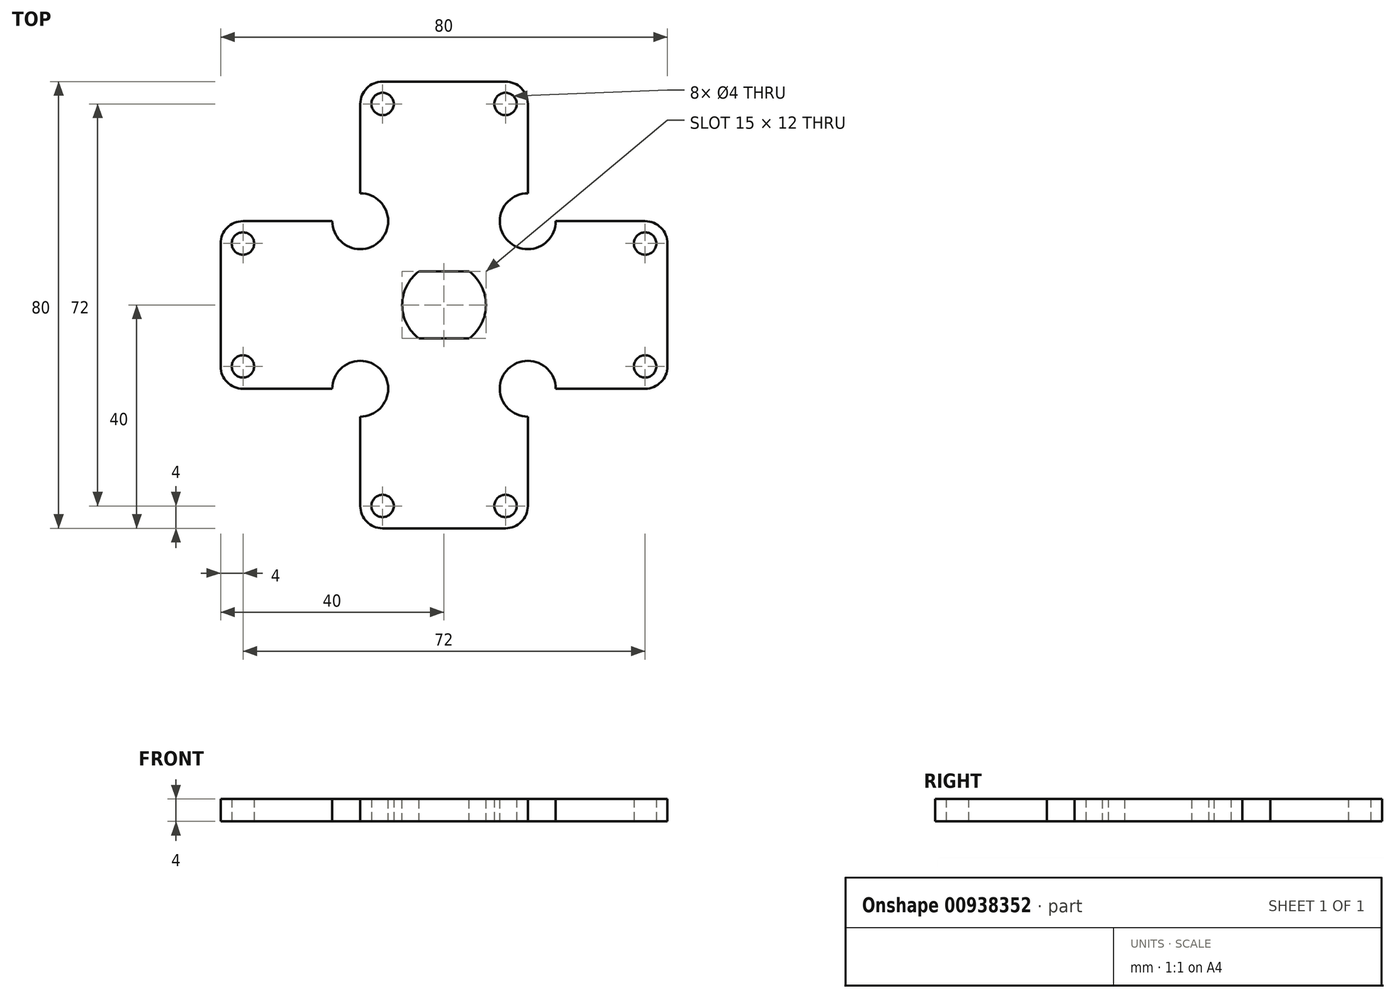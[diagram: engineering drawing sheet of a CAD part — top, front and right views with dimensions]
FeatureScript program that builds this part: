
annotation { "Feature Type Name" : "Feature", "Feature Type Description" : "" }
export const myFeature = defineFeature(function(context is Context, id is Id, definition is map)
    precondition{}
    {
        {
            var Q0;
            Q0=qCreatedBy(makeId("Top.planeOp"),FACE);
            var sketch = newSketch(context, id + "F0", { "sketchPlane" : qUnion([Q0])});
            skCircle(sketch, "E0", {"center": v(0, 0) * mm, "radius": 7.5 * mm, "construction": true});
            skLineSegment(sketch, "E1", {"start": v(-4.5, 6) * mm, "end": v(4.5, 6) * mm});
            skLineSegment(sketch, "E2", {"start": v(-4.5, -6) * mm, "end": v(4.5, -6) * mm});
            skArc(sketch, "E3", {"start": v(-4.5, 6) * mm, "mid": v(-7.5, 0) * mm, "end": v(-4.5, -6) * mm});
            skArc(sketch, "E4", {"start": v(4.5, 6) * mm, "mid": v(7.5, 0) * mm, "end": v(4.5, -6) * mm});
            skSolve(sketch);
        }
        {
            var Q0;
            Q0=qCreatedBy(makeId("Top.planeOp"),FACE);
            var sketch = newSketch(context, id + "F1", { "sketchPlane" : qUnion([Q0])});
            skLineSegment(sketch, "E5", {"start": v(0, 0) * mm, "end": v(-15, 15) * mm, "construction": true});
            skLineSegment(sketch, "E6", {"start": v(-15, 15) * mm, "end": v(-15, 36) * mm});
            skLineSegment(sketch, "E7", {"start": v(-11, 40) * mm, "end": v(0, 40) * mm});
            skArc(sketch, "E8", {"start": v(-15, 36) * mm, "mid": v(-13.83, 38.83) * mm, "end": v(-11, 40) * mm});
            skCircle(sketch, "E9", {"center": v(-11, 36) * mm, "radius": 2 * mm});
            skLineSegment(sketch, "E10.MirrorCS", {"start": v(11, 40) * mm, "end": v(0, 40) * mm});
            skArc(sketch, "E11.MirrorCS", {"start": v(15, 36) * mm, "mid": v(13.83, 38.83) * mm, "end": v(11, 40) * mm});
            skLineSegment(sketch, "E12.MirrorCS", {"start": v(15, 15) * mm, "end": v(15, 36) * mm});
            skCircle(sketch, "E13.MirrorC", {"center": v(11, 36) * mm, "radius": 2 * mm});
            skArc(sketch, "E14.1.0", {"start": v(-36, -15) * mm, "mid": v(-38.83, -13.83) * mm, "end": v(-40, -11) * mm});
            skLineSegment(sketch, "E14.1.1", {"start": v(-40, 11) * mm, "end": v(-40, 0) * mm});
            skArc(sketch, "E14.1.2", {"start": v(-36, 15) * mm, "mid": v(-38.83, 13.83) * mm, "end": v(-40, 11) * mm});
            skLineSegment(sketch, "E14.1.3", {"start": v(-15, 15) * mm, "end": v(-36, 15) * mm});
            skLineSegment(sketch, "E14.1.4", {"start": v(-40, -11) * mm, "end": v(-40, 0) * mm});
            skCircle(sketch, "E14.1.5", {"center": v(-36, -11) * mm, "radius": 2 * mm});
            skLineSegment(sketch, "E14.1.6", {"start": v(-15, -15) * mm, "end": v(-36, -15) * mm});
            skLineSegment(sketch, "E14.1.7", {"start": v(0, 0) * mm, "end": v(-15, -15) * mm, "construction": true});
            skCircle(sketch, "E14.1.8", {"center": v(-36, 11) * mm, "radius": 2 * mm});
            skArc(sketch, "E14.2.0", {"start": v(15, -36) * mm, "mid": v(13.83, -38.83) * mm, "end": v(11, -40) * mm});
            skLineSegment(sketch, "E14.2.1", {"start": v(-11, -40) * mm, "end": v(0, -40) * mm});
            skArc(sketch, "E14.2.2", {"start": v(-15, -36) * mm, "mid": v(-13.83, -38.83) * mm, "end": v(-11, -40) * mm});
            skLineSegment(sketch, "E14.2.3", {"start": v(-15, -15) * mm, "end": v(-15, -36) * mm});
            skLineSegment(sketch, "E14.2.4", {"start": v(11, -40) * mm, "end": v(0, -40) * mm});
            skCircle(sketch, "E14.2.5", {"center": v(11, -36) * mm, "radius": 2 * mm});
            skLineSegment(sketch, "E14.2.6", {"start": v(15, -15) * mm, "end": v(15, -36) * mm});
            skLineSegment(sketch, "E14.2.7", {"start": v(0, 0) * mm, "end": v(15, -15) * mm, "construction": true});
            skCircle(sketch, "E14.2.8", {"center": v(-11, -36) * mm, "radius": 2 * mm});
            skArc(sketch, "E14.3.0", {"start": v(36, 15) * mm, "mid": v(38.83, 13.83) * mm, "end": v(40, 11) * mm});
            skLineSegment(sketch, "E14.3.1", {"start": v(40, -11) * mm, "end": v(40, 0) * mm});
            skArc(sketch, "E14.3.2", {"start": v(36, -15) * mm, "mid": v(38.83, -13.83) * mm, "end": v(40, -11) * mm});
            skLineSegment(sketch, "E14.3.3", {"start": v(15, -15) * mm, "end": v(36, -15) * mm});
            skLineSegment(sketch, "E14.3.4", {"start": v(40, 11) * mm, "end": v(40, 0) * mm});
            skCircle(sketch, "E14.3.5", {"center": v(36, 11) * mm, "radius": 2 * mm});
            skLineSegment(sketch, "E14.3.6", {"start": v(15, 15) * mm, "end": v(36, 15) * mm});
            skLineSegment(sketch, "E14.3.7", {"start": v(0, 0) * mm, "end": v(15, 15) * mm, "construction": true});
            skCircle(sketch, "E14.3.8", {"center": v(36, -11) * mm, "radius": 2 * mm});
            skPoint(sketch, "E14.center", {"position": v(0, 0) * mm});
            skSolve(sketch);
        }
        {
            var Q0;
            Q0=qCreatedBy(makeId("Top.planeOp"),FACE);
            var sketch = newSketch(context, id + "F2", { "sketchPlane" : qUnion([Q0])});
            skCircle(sketch, "E15", {"center": v(-15, 15) * mm, "radius": 5 * mm});
            skCircle(sketch, "E16.1.0", {"center": v(-15, -15) * mm, "radius": 5 * mm});
            skCircle(sketch, "E16.2.0", {"center": v(15, -15) * mm, "radius": 5 * mm});
            skCircle(sketch, "E16.3.0", {"center": v(15, 15) * mm, "radius": 5 * mm});
            skPoint(sketch, "E16.center", {"position": v(0, 0) * mm});
            skSolve(sketch);
        }
        {
            var Q0;
            Q0 = qSketchRegion(id + "F1", true);
            extrude(context, id + "F3", {"entities" : qUnion([Q0]), "endBound" : BoundingType.SYMMETRIC, "depth" : 4 * mm, "offsetDistance" : 25 * mm});
        }
        {
            var Q0;
            Q0 = qSketchRegion(id + "F0", true);
            extrude(context, id + "F4", {"entities" : qUnion([Q0]), "operationType" : NewBodyOperationType.REMOVE, "endBound" : BoundingType.THROUGH_ALL, "oppositeDirection" : true, "depth" : 25 * mm, "offsetDistance" : 25 * mm, "hasSecondDirection" : true, "secondDirectionBound" : SecondDirectionBoundingType.THROUGH_ALL, "secondDirectionOppositeDirection" : false, "secondDirectionDepth" : 25 * mm});
        }
        {
            var Q0;
            Q0 = qSketchRegion(id + "F2", true);
            extrude(context, id + "F5", {"entities" : qUnion([Q0]), "operationType" : NewBodyOperationType.REMOVE, "endBound" : BoundingType.THROUGH_ALL, "oppositeDirection" : true, "depth" : 25 * mm, "offsetDistance" : 25 * mm, "hasSecondDirection" : true, "secondDirectionBound" : SecondDirectionBoundingType.THROUGH_ALL, "secondDirectionOppositeDirection" : false, "secondDirectionDepth" : 25 * mm});
        }
    });
